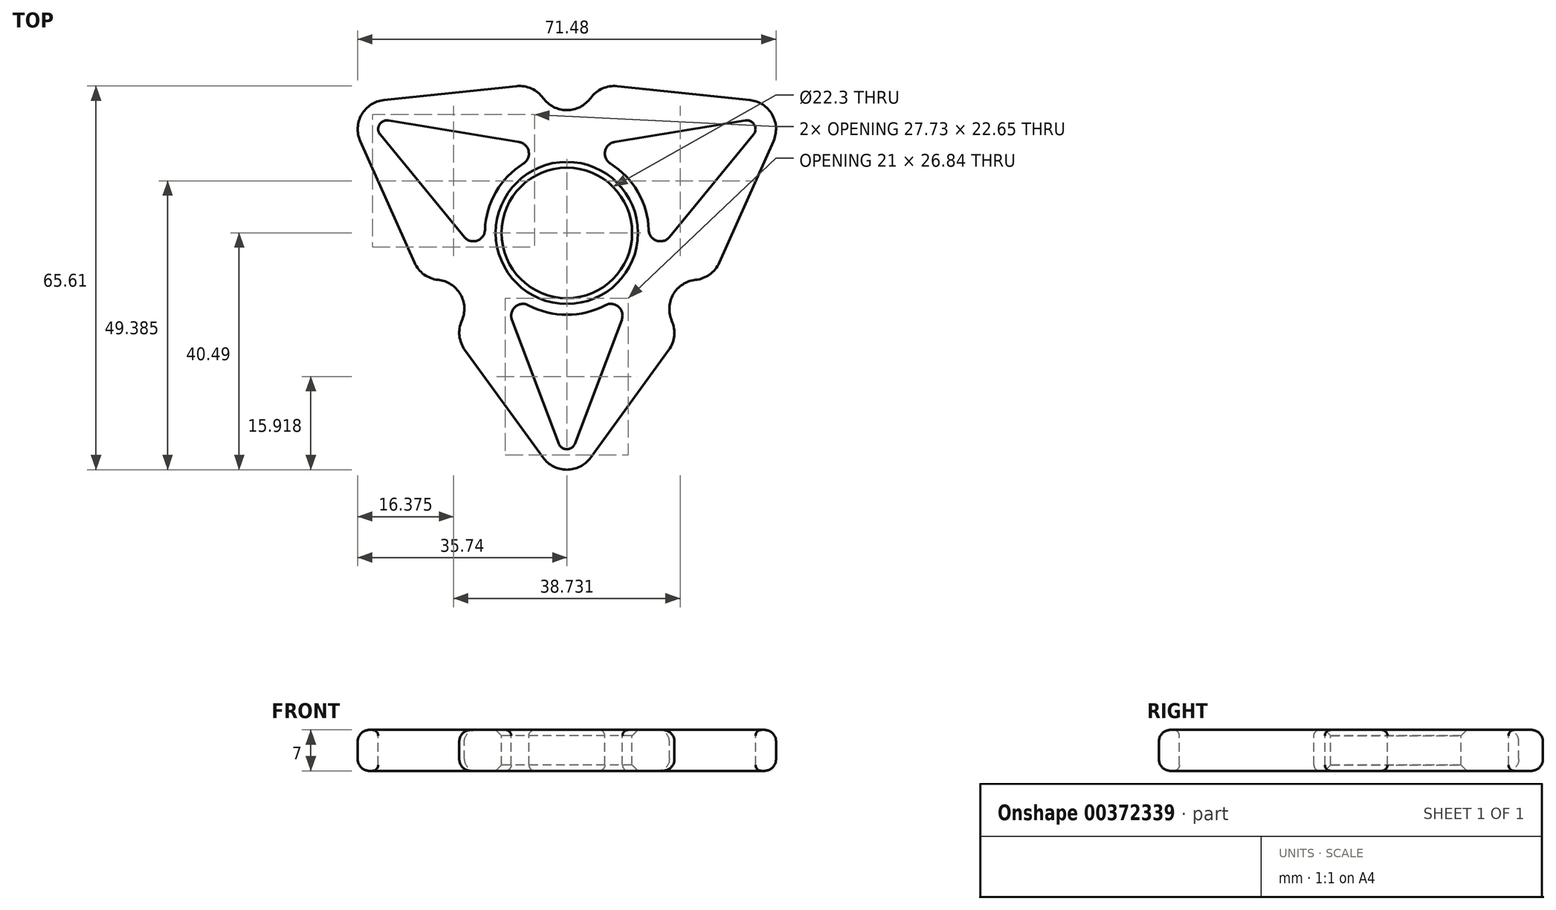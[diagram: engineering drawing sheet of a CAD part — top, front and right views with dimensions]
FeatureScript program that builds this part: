
annotation { "Feature Type Name" : "Feature", "Feature Type Description" : "" }
export const myFeature = defineFeature(function(context is Context, id is Id, definition is map)
    precondition{}
    {
        {
            var Q0;
            Q0=qCreatedBy(makeId("Top.planeOp"),FACE);
            var sketch = newSketch(context, id + "F0", { "sketchPlane" : qUnion([Q0])});
            skCircle(sketch, "E0.cCircle", {"center": v(0, 0) * mm, "radius": 22 * mm, "construction": true});
            skLineSegment(sketch, "E0.0", {"start": v(-38.1, 22) * mm, "end": v(38.1, 22) * mm});
            skLineSegment(sketch, "E0.1", {"start": v(38.1, 22) * mm, "end": v(0, -44) * mm});
            skLineSegment(sketch, "E0.2", {"start": v(0, -44) * mm, "end": v(-38.1, 22) * mm});
            skPoint(sketch, "E0.0.midPoint", {"position": v(0, 22) * mm});
            skLineSegment(sketch, "E1", {"start": v(-38.1, 22) * mm, "end": v(0, 26) * mm});
            skLineSegment(sketch, "E2", {"start": v(0, 26) * mm, "end": v(38.1, 22) * mm});
            skLineSegment(sketch, "E3.1.0", {"start": v(0, -44) * mm, "end": v(-22.52, -13) * mm});
            skLineSegment(sketch, "E3.1.1", {"start": v(-22.52, -13) * mm, "end": v(-38.1, 22) * mm});
            skLineSegment(sketch, "E3.2.0", {"start": v(38.1, 22) * mm, "end": v(22.52, -13) * mm});
            skLineSegment(sketch, "E3.2.1", {"start": v(22.52, -13) * mm, "end": v(0, -44) * mm});
            skSolve(sketch);
        }
        {
            var Q0;
            Q0=qSketchRegion(id+"F0",true);
            extrude(context, id + "F1", {"entities" : qUnion([Q0]), "depth" : 7 * mm});
        }
        {
            var Q0;
            Q0=makeQuery(id+"F1.opExtrude","CAP_FACE",FACE,{"disambiguationData":[OSD([sQuery(id+"F0.wireOp",EDGE,"E1"),sQuery(id+"F0.wireOp",EDGE,"E2"),sQuery(id+"F0.wireOp",EDGE,"E3.1.0"),sQuery(id+"F0.wireOp",EDGE,"E3.1.1"),sQuery(id+"F0.wireOp",EDGE,"E3.2.0"),sQuery(id+"F0.wireOp",EDGE,"E3.2.1")])],"isStart":false});
            var sketch = newSketch(context, id + "F2", { "sketchPlane" : qUnion([Q0])});
            skCircle(sketch, "E4", {"center": v(0, 0) * mm, "radius": 11.15 * mm});
            skSolve(sketch);
        }
        {
            var Q0;
            Q0=qSketchRegion(id+"F2",true);
            extrude(context, id + "F3", {"entities" : qUnion([Q0]), "operationType" : NewBodyOperationType.REMOVE, "endBound" : BoundingType.THROUGH_ALL, "oppositeDirection" : true, "depth" : 25 * mm});
        }
        {
            var Q0;
            Q0=makeQuery(id+"F1.opExtrude","SWEPT_EDGE",EDGE,{"disambiguationData":[OSD([sQuery(id+"F0.wireOp",EDGE,"E0.1"),sQuery(id+"F0.wireOp",EDGE,"E0.2"),sQuery(id+"F0.wireOp",EDGE,"E3.1.0"),sQuery(id+"F0.wireOp",EDGE,"E3.2.1")])]});
            var Q1;
            Q1=makeQuery(id+"F1.opExtrude","SWEPT_EDGE",EDGE,{"disambiguationData":[OSD([sQuery(id+"F0.wireOp",EDGE,"E0.0"),sQuery(id+"F0.wireOp",EDGE,"E0.2"),sQuery(id+"F0.wireOp",EDGE,"E1"),sQuery(id+"F0.wireOp",EDGE,"E3.1.1")])]});
            var Q2;
            Q2=makeQuery(id+"F1.opExtrude","SWEPT_EDGE",EDGE,{"disambiguationData":[OSD([sQuery(id+"F0.wireOp",EDGE,"E0.0"),sQuery(id+"F0.wireOp",EDGE,"E0.1"),sQuery(id+"F0.wireOp",EDGE,"E2"),sQuery(id+"F0.wireOp",EDGE,"E3.2.0")])]});
            fillet(context, id + "F4", {"entities" : qUnion([Q0, Q1, Q2]), "radius" : 5 * mm, "tangentPropagation" : true, "allowEdgeOverflow" : false});
        }
        {
            var Q0;
            Q0=makeQuery(id+"F1.opExtrude","CAP_FACE",FACE,{"disambiguationData":[OSD([sQuery(id+"F0.wireOp",EDGE,"E1"),sQuery(id+"F0.wireOp",EDGE,"E2"),sQuery(id+"F0.wireOp",EDGE,"E3.1.0"),sQuery(id+"F0.wireOp",EDGE,"E3.1.1"),sQuery(id+"F0.wireOp",EDGE,"E3.2.0"),sQuery(id+"F0.wireOp",EDGE,"E3.2.1")])],"isStart":false});
            var sketch = newSketch(context, id + "F5", { "sketchPlane" : qUnion([Q0])});
            skArc(sketch, "E5", {"start": v(-4.05, 23.06) * mm, "mid": v(0, 21) * mm, "end": v(4.05, 23.06) * mm});
            skLineSegment(sketch, "E6", {"start": v(-31.26, 22.72) * mm, "end": v(-8.61, 25.1) * mm});
            skLineSegment(sketch, "E7", {"start": v(8.61, 25.1) * mm, "end": v(31.26, 22.72) * mm});
            skPoint(sketch, "E8.visualSharp", {"position": v(-4.97, 25.48) * mm});
            skArc(sketch, "E8.filletArc", {"start": v(-4.05, 23.06) * mm, "mid": v(-6.06, 24.7) * mm, "end": v(-8.61, 25.1) * mm});
            skPoint(sketch, "E9.visualSharp", {"position": v(4.97, 25.48) * mm});
            skArc(sketch, "E9.filletArc", {"start": v(8.61, 25.1) * mm, "mid": v(6.06, 24.7) * mm, "end": v(4.05, 23.06) * mm});
            skLineSegment(sketch, "E10", {"start": v(-8.61, 25.1) * mm, "end": v(0, 26) * mm});
            skLineSegment(sketch, "E11", {"start": v(8.61, 25.1) * mm, "end": v(0, 26) * mm});
            skLineSegment(sketch, "E12.1.0", {"start": v(-4.05, -38.43) * mm, "end": v(-17.43, -20) * mm});
            skLineSegment(sketch, "E12.1.1", {"start": v(-26.04, -5.09) * mm, "end": v(-35.3, 15.71) * mm});
            skPoint(sketch, "E12.1.2", {"position": v(-24.55, -8.43) * mm});
            skLineSegment(sketch, "E12.1.3", {"start": v(-17.43, -20) * mm, "end": v(-22.52, -13) * mm});
            skLineSegment(sketch, "E12.1.4", {"start": v(-26.04, -5.09) * mm, "end": v(-22.52, -13) * mm});
            skPoint(sketch, "E12.1.5", {"position": v(-19.58, -17.05) * mm});
            skArc(sketch, "E12.1.6", {"start": v(-17.95, -15.03) * mm, "mid": v(-18.19, -10.5) * mm, "end": v(-22, -8.03) * mm});
            skArc(sketch, "E12.1.7", {"start": v(-17.95, -15.03) * mm, "mid": v(-18.35, -17.6) * mm, "end": v(-17.43, -20) * mm});
            skArc(sketch, "E12.1.8", {"start": v(-26.04, -5.09) * mm, "mid": v(-24.41, -7.1) * mm, "end": v(-22, -8.03) * mm});
            skLineSegment(sketch, "E12.2.0", {"start": v(35.3, 15.71) * mm, "end": v(26.04, -5.09) * mm});
            skLineSegment(sketch, "E12.2.1", {"start": v(17.43, -20) * mm, "end": v(4.05, -38.43) * mm});
            skPoint(sketch, "E12.2.2", {"position": v(19.58, -17.05) * mm});
            skLineSegment(sketch, "E12.2.3", {"start": v(26.04, -5.09) * mm, "end": v(22.52, -13) * mm});
            skLineSegment(sketch, "E12.2.4", {"start": v(17.43, -20) * mm, "end": v(22.52, -13) * mm});
            skPoint(sketch, "E12.2.5", {"position": v(24.55, -8.43) * mm});
            skArc(sketch, "E12.2.6", {"start": v(22, -8.03) * mm, "mid": v(18.19, -10.5) * mm, "end": v(17.95, -15.03) * mm});
            skArc(sketch, "E12.2.7", {"start": v(22, -8.03) * mm, "mid": v(24.41, -7.1) * mm, "end": v(26.04, -5.09) * mm});
            skArc(sketch, "E12.2.8", {"start": v(17.43, -20) * mm, "mid": v(18.35, -17.6) * mm, "end": v(17.95, -15.03) * mm});
            skPoint(sketch, "E12.center", {"position": v(0, 0) * mm});
            skSolve(sketch);
        }
        {
            var Q0;
            Q0=qSketchRegion(id+"F5",true);
            extrude(context, id + "F6", {"entities" : qUnion([Q0]), "operationType" : NewBodyOperationType.REMOVE, "endBound" : BoundingType.THROUGH_ALL, "oppositeDirection" : true, "depth" : 25 * mm});
        }
        {
            var Q0;
            Q0=makeQuery(id+"F1.opExtrude","CAP_FACE",FACE,{"disambiguationData":[OSD([sQuery(id+"F0.wireOp",EDGE,"E1"),sQuery(id+"F0.wireOp",EDGE,"E2"),sQuery(id+"F0.wireOp",EDGE,"E3.1.0"),sQuery(id+"F0.wireOp",EDGE,"E3.1.1"),sQuery(id+"F0.wireOp",EDGE,"E3.2.0"),sQuery(id+"F0.wireOp",EDGE,"E3.2.1")])],"isStart":false});
            var sketch = newSketch(context, id + "F7", { "sketchPlane" : qUnion([Q0])});
            skArc(sketch, "E13", {"start": v(-1.4, -36.02) * mm, "mid": v(0, -37) * mm, "end": v(1.4, -36.02) * mm});
            skArc(sketch, "E14", {"start": v(-6.57, -12.36) * mm, "mid": v(0, -14) * mm, "end": v(6.57, -12.36) * mm});
            skLineSegment(sketch, "E15", {"start": v(-9.38, -14.84) * mm, "end": v(-1.4, -36.02) * mm});
            skLineSegment(sketch, "E16", {"start": v(9.38, -14.84) * mm, "end": v(1.4, -36.02) * mm});
            skPoint(sketch, "E17.visualSharp", {"position": v(-13.1, -4.93) * mm});
            skArc(sketch, "E17.filletArc", {"start": v(-6.57, -12.36) * mm, "mid": v(-8.82, -12.63) * mm, "end": v(-9.38, -14.84) * mm});
            skPoint(sketch, "E18.visualSharp", {"position": v(13.1, -4.93) * mm});
            skArc(sketch, "E18.filletArc", {"start": v(9.38, -14.84) * mm, "mid": v(8.82, -12.63) * mm, "end": v(6.57, -12.36) * mm});
            skArc(sketch, "E19.1.0", {"start": v(14, 0.5) * mm, "mid": v(12.12, 7) * mm, "end": v(7.43, 11.87) * mm});
            skArc(sketch, "E19.1.1", {"start": v(8.16, 15.54) * mm, "mid": v(6.53, 13.96) * mm, "end": v(7.43, 11.87) * mm});
            skPoint(sketch, "E19.1.2", {"position": v(10.82, -8.88) * mm});
            skPoint(sketch, "E19.1.3", {"position": v(-2.28, 13.81) * mm});
            skLineSegment(sketch, "E19.1.4", {"start": v(8.16, 15.54) * mm, "end": v(30.5, 19.23) * mm});
            skArc(sketch, "E19.1.5", {"start": v(14, 0.5) * mm, "mid": v(15.35, -1.33) * mm, "end": v(17.54, -0.7) * mm});
            skLineSegment(sketch, "E19.1.6", {"start": v(17.54, -0.7) * mm, "end": v(31.9, 16.8) * mm});
            skArc(sketch, "E19.1.7", {"start": v(31.9, 16.8) * mm, "mid": v(32.04, 18.5) * mm, "end": v(30.5, 19.23) * mm});
            skArc(sketch, "E19.2.0", {"start": v(-7.43, 11.87) * mm, "mid": v(-12.12, 7) * mm, "end": v(-14, 0.5) * mm});
            skArc(sketch, "E19.2.1", {"start": v(-17.54, -0.7) * mm, "mid": v(-15.35, -1.33) * mm, "end": v(-14, 0.5) * mm});
            skPoint(sketch, "E19.2.2", {"position": v(2.28, 13.81) * mm});
            skPoint(sketch, "E19.2.3", {"position": v(-10.82, -8.88) * mm});
            skLineSegment(sketch, "E19.2.4", {"start": v(-17.54, -0.7) * mm, "end": v(-31.9, 16.8) * mm});
            skArc(sketch, "E19.2.5", {"start": v(-7.43, 11.87) * mm, "mid": v(-6.53, 13.96) * mm, "end": v(-8.16, 15.54) * mm});
            skLineSegment(sketch, "E19.2.6", {"start": v(-8.16, 15.54) * mm, "end": v(-30.5, 19.23) * mm});
            skArc(sketch, "E19.2.7", {"start": v(-30.5, 19.23) * mm, "mid": v(-32.04, 18.5) * mm, "end": v(-31.9, 16.8) * mm});
            skSolve(sketch);
        }
        {
            var Q0;
            Q0=makeQuery(id+"F4.opFillet","BLEND_FACE",FACE,{"disambiguationData":[OSD([sQuery(id+"F0.wireOp",EDGE,"E0.0"),sQuery(id+"F0.wireOp",EDGE,"E0.2"),sQuery(id+"F0.wireOp",EDGE,"E1"),sQuery(id+"F0.wireOp",EDGE,"E3.1.1")])]});
            var Q1;
            Q1=makeQuery(id+"F1.opExtrude","SWEPT_FACE",FACE,{"disambiguationData":[OSD([sQuery(id+"F0.wireOp",EDGE,"E3.1.1")])]});
            var Q2;
            Q2=makeQuery(id+"F6.boolean.opBoolean","COPY",FACE,{"derivedFrom":makeQuery(id+"F6.opExtrude","SWEPT_FACE",FACE,{"disambiguationData":[OSD([sQuery(id+"F5.wireOp",EDGE,"E12.1.8")])]})});
            var Q3;
            Q3=makeQuery(id+"F6.boolean.opBoolean","COPY",FACE,{"derivedFrom":makeQuery(id+"F6.opExtrude","SWEPT_FACE",FACE,{"disambiguationData":[OSD([sQuery(id+"F5.wireOp",EDGE,"E12.1.6")])]})});
            var Q4;
            Q4=makeQuery(id+"F6.boolean.opBoolean","COPY",FACE,{"derivedFrom":makeQuery(id+"F6.opExtrude","SWEPT_FACE",FACE,{"disambiguationData":[OSD([sQuery(id+"F5.wireOp",EDGE,"E12.1.7")])]})});
            var Q5;
            Q5=makeQuery(id+"F1.opExtrude","SWEPT_FACE",FACE,{"disambiguationData":[OSD([sQuery(id+"F0.wireOp",EDGE,"E3.1.0")])]});
            var Q6;
            Q6=makeQuery(id+"F4.opFillet","BLEND_FACE",FACE,{"disambiguationData":[OSD([sQuery(id+"F0.wireOp",EDGE,"E0.1"),sQuery(id+"F0.wireOp",EDGE,"E0.2"),sQuery(id+"F0.wireOp",EDGE,"E3.1.0"),sQuery(id+"F0.wireOp",EDGE,"E3.2.1")])]});
            var Q7;
            Q7=makeQuery(id+"F1.opExtrude","SWEPT_FACE",FACE,{"disambiguationData":[OSD([sQuery(id+"F0.wireOp",EDGE,"E3.2.1")])]});
            var Q8;
            Q8=makeQuery(id+"F6.boolean.opBoolean","COPY",FACE,{"derivedFrom":makeQuery(id+"F6.opExtrude","SWEPT_FACE",FACE,{"disambiguationData":[OSD([sQuery(id+"F5.wireOp",EDGE,"E12.2.8")])]})});
            var Q9;
            Q9=makeQuery(id+"F6.boolean.opBoolean","COPY",FACE,{"derivedFrom":makeQuery(id+"F6.opExtrude","SWEPT_FACE",FACE,{"disambiguationData":[OSD([sQuery(id+"F5.wireOp",EDGE,"E12.2.6")])]})});
            var Q10;
            Q10=makeQuery(id+"F6.boolean.opBoolean","COPY",FACE,{"derivedFrom":makeQuery(id+"F6.opExtrude","SWEPT_FACE",FACE,{"disambiguationData":[OSD([sQuery(id+"F5.wireOp",EDGE,"E12.2.7")])]})});
            var Q11;
            Q11=makeQuery(id+"F1.opExtrude","SWEPT_FACE",FACE,{"disambiguationData":[OSD([sQuery(id+"F0.wireOp",EDGE,"E3.2.0")])]});
            var Q12;
            Q12=makeQuery(id+"F4.opFillet","BLEND_FACE",FACE,{"disambiguationData":[OSD([sQuery(id+"F0.wireOp",EDGE,"E0.0"),sQuery(id+"F0.wireOp",EDGE,"E0.1"),sQuery(id+"F0.wireOp",EDGE,"E2"),sQuery(id+"F0.wireOp",EDGE,"E3.2.0")])]});
            var Q13;
            Q13=makeQuery(id+"F1.opExtrude","SWEPT_FACE",FACE,{"disambiguationData":[OSD([sQuery(id+"F0.wireOp",EDGE,"E2")])]});
            var Q14;
            Q14=makeQuery(id+"F6.boolean.opBoolean","COPY",FACE,{"derivedFrom":makeQuery(id+"F6.opExtrude","SWEPT_FACE",FACE,{"disambiguationData":[OSD([sQuery(id+"F5.wireOp",EDGE,"E9.filletArc")])]})});
            var Q15;
            Q15=makeQuery(id+"F6.boolean.opBoolean","COPY",FACE,{"derivedFrom":makeQuery(id+"F6.opExtrude","SWEPT_FACE",FACE,{"disambiguationData":[OSD([sQuery(id+"F5.wireOp",EDGE,"E5")])]})});
            var Q16;
            Q16=makeQuery(id+"F6.boolean.opBoolean","COPY",FACE,{"derivedFrom":makeQuery(id+"F6.opExtrude","SWEPT_FACE",FACE,{"disambiguationData":[OSD([sQuery(id+"F5.wireOp",EDGE,"E8.filletArc")])]})});
            var Q17;
            Q17=makeQuery(id+"F1.opExtrude","SWEPT_FACE",FACE,{"disambiguationData":[OSD([sQuery(id+"F0.wireOp",EDGE,"E1")])]});
            fillet(context, id + "F8", {"entities" : qUnion([Q0, Q1, Q2, Q3, Q4, Q5, Q6, Q7, Q8, Q9, Q10, Q11, Q12, Q13, Q14, Q15, Q16, Q17]), "radius" : 2 * mm, "tangentPropagation" : true, "allowEdgeOverflow" : false});
        }
        {
            var Q0;
            Q0=qSketchRegion(id+"F7",true);
            extrude(context, id + "F9", {"entities" : qUnion([Q0]), "operationType" : NewBodyOperationType.REMOVE, "endBound" : BoundingType.THROUGH_ALL, "oppositeDirection" : true, "depth" : 25 * mm});
        }
        {
            var Q0;
            Q0=makeQuery(id+"F9.boolean.opBoolean","COPY",FACE,{"derivedFrom":makeQuery(id+"F9.opExtrude","SWEPT_FACE",FACE,{"disambiguationData":[OSD([sQuery(id+"F7.wireOp",EDGE,"E19.1.7")])]})});
            var Q1;
            Q1=makeQuery(id+"F9.boolean.opBoolean","COPY",FACE,{"derivedFrom":makeQuery(id+"F9.opExtrude","SWEPT_FACE",FACE,{"disambiguationData":[OSD([sQuery(id+"F7.wireOp",EDGE,"E19.1.4")])]})});
            var Q2;
            Q2=makeQuery(id+"F9.boolean.opBoolean","COPY",FACE,{"derivedFrom":makeQuery(id+"F9.opExtrude","SWEPT_FACE",FACE,{"disambiguationData":[OSD([sQuery(id+"F7.wireOp",EDGE,"E19.2.6")])]})});
            var Q3;
            Q3=makeQuery(id+"F9.boolean.opBoolean","COPY",FACE,{"derivedFrom":makeQuery(id+"F9.opExtrude","SWEPT_FACE",FACE,{"disambiguationData":[OSD([sQuery(id+"F7.wireOp",EDGE,"E19.2.5")])]})});
            var Q4;
            Q4=makeQuery(id+"F9.boolean.opBoolean","COPY",FACE,{"derivedFrom":makeQuery(id+"F9.opExtrude","SWEPT_FACE",FACE,{"disambiguationData":[OSD([sQuery(id+"F7.wireOp",EDGE,"E19.2.0")])]})});
            var Q5;
            Q5=makeQuery(id+"F9.boolean.opBoolean","COPY",FACE,{"derivedFrom":makeQuery(id+"F9.opExtrude","SWEPT_FACE",FACE,{"disambiguationData":[OSD([sQuery(id+"F7.wireOp",EDGE,"E19.1.6")])]})});
            var Q6;
            Q6=makeQuery(id+"F9.boolean.opBoolean","COPY",FACE,{"derivedFrom":makeQuery(id+"F9.opExtrude","SWEPT_FACE",FACE,{"disambiguationData":[OSD([sQuery(id+"F7.wireOp",EDGE,"E14")])]})});
            var Q7;
            Q7=makeQuery(id+"F9.boolean.opBoolean","COPY",FACE,{"derivedFrom":makeQuery(id+"F9.opExtrude","SWEPT_FACE",FACE,{"disambiguationData":[OSD([sQuery(id+"F7.wireOp",EDGE,"E18.filletArc")])]})});
            var Q8;
            Q8=makeQuery(id+"F9.boolean.opBoolean","COPY",FACE,{"derivedFrom":makeQuery(id+"F9.opExtrude","SWEPT_FACE",FACE,{"disambiguationData":[OSD([sQuery(id+"F7.wireOp",EDGE,"E16")])]})});
            var Q9;
            Q9=makeQuery(id+"F9.boolean.opBoolean","COPY",FACE,{"derivedFrom":makeQuery(id+"F9.opExtrude","SWEPT_FACE",FACE,{"disambiguationData":[OSD([sQuery(id+"F7.wireOp",EDGE,"E19.2.4")])]})});
            var Q10;
            Q10=makeQuery(id+"F9.boolean.opBoolean","COPY",FACE,{"derivedFrom":makeQuery(id+"F9.opExtrude","SWEPT_FACE",FACE,{"disambiguationData":[OSD([sQuery(id+"F7.wireOp",EDGE,"E19.1.0")])]})});
            var Q11;
            Q11=makeQuery(id+"F9.boolean.opBoolean","COPY",FACE,{"derivedFrom":makeQuery(id+"F9.opExtrude","SWEPT_FACE",FACE,{"disambiguationData":[OSD([sQuery(id+"F7.wireOp",EDGE,"E19.1.1")])]})});
            var Q12;
            Q12=makeQuery(id+"F9.boolean.opBoolean","COPY",FACE,{"derivedFrom":makeQuery(id+"F9.opExtrude","SWEPT_FACE",FACE,{"disambiguationData":[OSD([sQuery(id+"F7.wireOp",EDGE,"E15")])]})});
            var Q13;
            Q13=makeQuery(id+"F9.boolean.opBoolean","COPY",FACE,{"derivedFrom":makeQuery(id+"F9.opExtrude","SWEPT_FACE",FACE,{"disambiguationData":[OSD([sQuery(id+"F7.wireOp",EDGE,"E19.2.7")])]})});
            var Q14;
            Q14=makeQuery(id+"F9.boolean.opBoolean","COPY",FACE,{"derivedFrom":makeQuery(id+"F9.opExtrude","SWEPT_FACE",FACE,{"disambiguationData":[OSD([sQuery(id+"F7.wireOp",EDGE,"E17.filletArc")])]})});
            var Q15;
            Q15=makeQuery(id+"F9.boolean.opBoolean","COPY",FACE,{"derivedFrom":makeQuery(id+"F9.opExtrude","SWEPT_FACE",FACE,{"disambiguationData":[OSD([sQuery(id+"F7.wireOp",EDGE,"E19.2.1")])]})});
            var Q16;
            Q16=makeQuery(id+"F9.boolean.opBoolean","COPY",FACE,{"derivedFrom":makeQuery(id+"F9.opExtrude","SWEPT_FACE",FACE,{"disambiguationData":[OSD([sQuery(id+"F7.wireOp",EDGE,"E19.1.5")])]})});
            var Q17;
            Q17=makeQuery(id+"F9.boolean.opBoolean","COPY",FACE,{"derivedFrom":makeQuery(id+"F9.opExtrude","SWEPT_FACE",FACE,{"disambiguationData":[OSD([sQuery(id+"F7.wireOp",EDGE,"E13")])]})});
            fillet(context, id + "F10", {"entities" : qUnion([Q0, Q1, Q2, Q3, Q4, Q5, Q6, Q7, Q8, Q9, Q10, Q11, Q12, Q13, Q14, Q15, Q16, Q17]), "radius" : 1 * mm, "tangentPropagation" : true, "allowEdgeOverflow" : false});
        }
        {
            var Q0;
            Q0=makeQuery(id+"F3.boolean.opBoolean","COPY",FACE,{"derivedFrom":makeQuery(id+"F3.opExtrude","SWEPT_FACE",FACE,{"disambiguationData":[OSD([sQuery(id+"F2.wireOp",EDGE,"E4")])]})});
            chamfer(context, id + "F11", {"entities" : qUnion([Q0]), "width" : 1 * mm, "tangentPropagation" : true});
        }
    });
